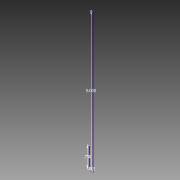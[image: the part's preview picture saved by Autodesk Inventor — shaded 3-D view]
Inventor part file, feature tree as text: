
AUTODESK INVENTOR PART (.ipt)
format: ipt  version: 2013 (Build 170138000, 138)  size: 57,856 bytes
history: native  units: in
note: dims shown in document units (in); Inventor stores cm internally (conversion verified against a paired STEP export)
features: sketch x1
ambient origin geometry x8: Origin, YZ Plane, XZ Plane, XY Plane, X Axis, Y Axis, Z Axis, Center Point
feature tree (1):
  sketch  "Sketch1"  dims[d6=0.75in d7=0.125in d8=5.0in]
